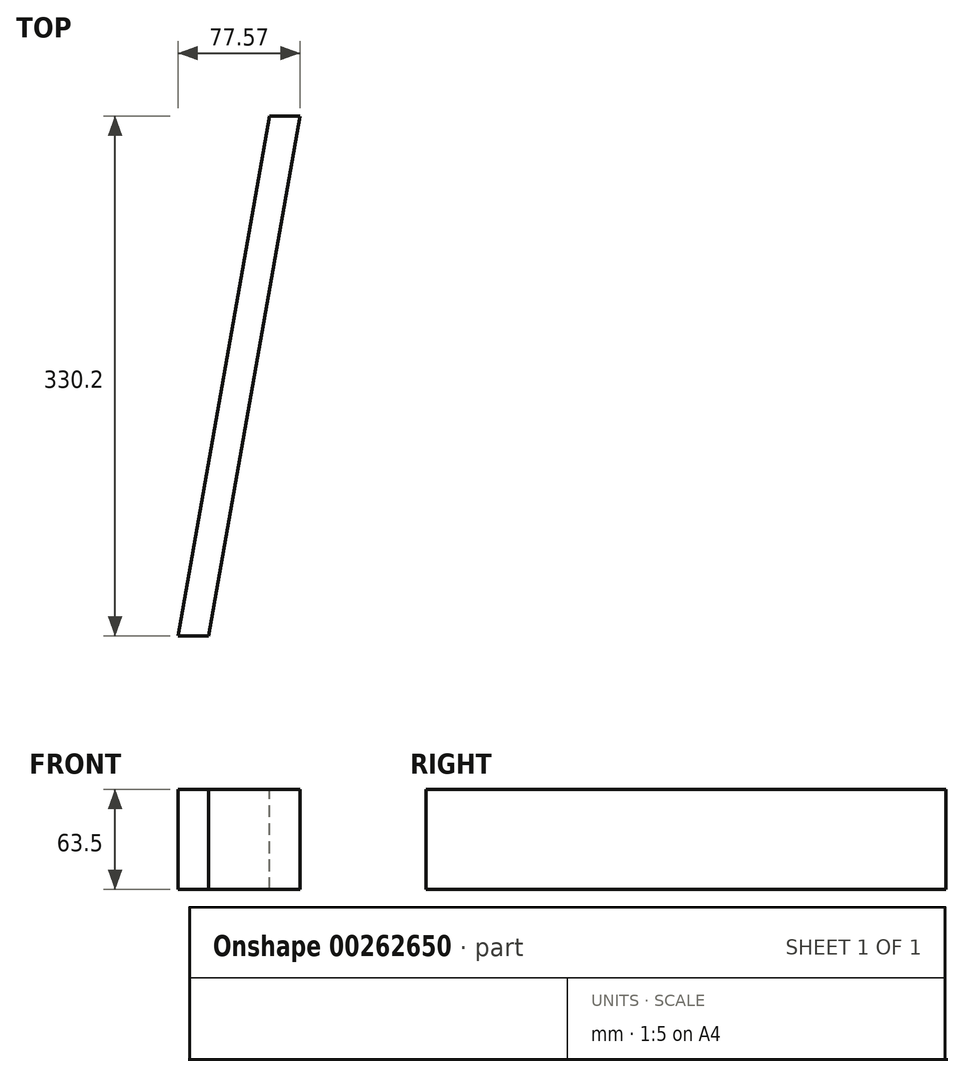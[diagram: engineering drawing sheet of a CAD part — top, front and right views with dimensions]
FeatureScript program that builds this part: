
annotation { "Feature Type Name" : "Feature", "Feature Type Description" : "" }
export const myFeature = defineFeature(function(context is Context, id is Id, definition is map)
    precondition{}
    {
        {
            var Q0;
            Q0=qCreatedBy(makeId("Top.planeOp"),FACE);
            var sketch = newSketch(context, id + "F0", { "sketchPlane" : qUnion([Q0])});
            skLineSegment(sketch, "E0", {"start": v(0, 202.27) * mm, "end": v(0, -71.47) * mm});
            skLineSegment(sketch, "E1", {"start": v(0, 202.27) * mm, "end": v(-132.32, -548.16) * mm});
            skLineSegment(sketch, "E2", {"start": v(-132.32, -548.16) * mm, "end": v(-151.08, -544.85) * mm});
            skLineSegment(sketch, "E3", {"start": v(-151.08, -544.85) * mm, "end": v(-18.76, 205.57) * mm});
            skLineSegment(sketch, "E4", {"start": v(0, 202.27) * mm, "end": v(-18.76, 205.57) * mm});
            skSolve(sketch);
        }
        {
            var Q0;
            Q0=makeQuery(id+"F0.imprint","IMPRINT",FACE,{"disambiguationData":[TD([[makeQuery(id+"F0.imprint","IMPRINT",EDGE,{"derivedFrom":sQuery(id+"F0.wireOp",EDGE,"E1")}),-1.0]])]});
            extrude(context, id + "F1", {"entities" : qUnion([Q0]), "depth" : 203.2 * mm, "offsetDistance" : 25.4 * mm});
        }
        {
            var Q0;
            Q0=qCreatedBy(makeId("Right.planeOp"),FACE);
            var sketch = newSketch(context, id + "F2", { "sketchPlane" : qUnion([Q0])});
            skLineSegment(sketch, "E5", {"start": v(0, 0) * mm, "end": v(221.93, 0) * mm});
            skLineSegment(sketch, "E6.bottom", {"start": v(-595.23, 248.04) * mm, "end": v(250.1, 248.04) * mm});
            skLineSegment(sketch, "E6.top", {"start": v(-595.23, -50.8) * mm, "end": v(250.1, -50.8) * mm});
            skLineSegment(sketch, "E6.left", {"start": v(-595.23, 248.04) * mm, "end": v(-595.23, -50.8) * mm});
            skLineSegment(sketch, "E6.right", {"start": v(250.1, 248.04) * mm, "end": v(250.1, -50.8) * mm});
            skLineSegment(sketch, "E7", {"start": v(-392.79, 12.7) * mm, "end": v(-392.79, 76.2) * mm});
            skLineSegment(sketch, "E8", {"start": v(-392.79, 76.2) * mm, "end": v(-62.59, 76.2) * mm});
            skLineSegment(sketch, "E9", {"start": v(-62.59, 76.2) * mm, "end": v(-62.59, 12.7) * mm});
            skLineSegment(sketch, "E10", {"start": v(-392.79, 12.7) * mm, "end": v(-62.59, 12.7) * mm});
            skSolve(sketch);
        }
        {
            var Q0;
            Q0=makeQuery(id+"F2.imprint","IMPRINT",FACE,{"disambiguationData":[TD([[makeQuery(id+"F2.imprint","IMPRINT",EDGE,{"derivedFrom":sQuery(id+"F2.wireOp",EDGE,"E6.bottom")}),-1.0]])]});
            extrude(context, id + "F3", {"entities" : qUnion([Q0]), "operationType" : NewBodyOperationType.REMOVE, "endBound" : BoundingType.THROUGH_ALL, "oppositeDirection" : true, "depth" : 25.4 * mm, "offsetDistance" : 25.4 * mm});
        }
    });
